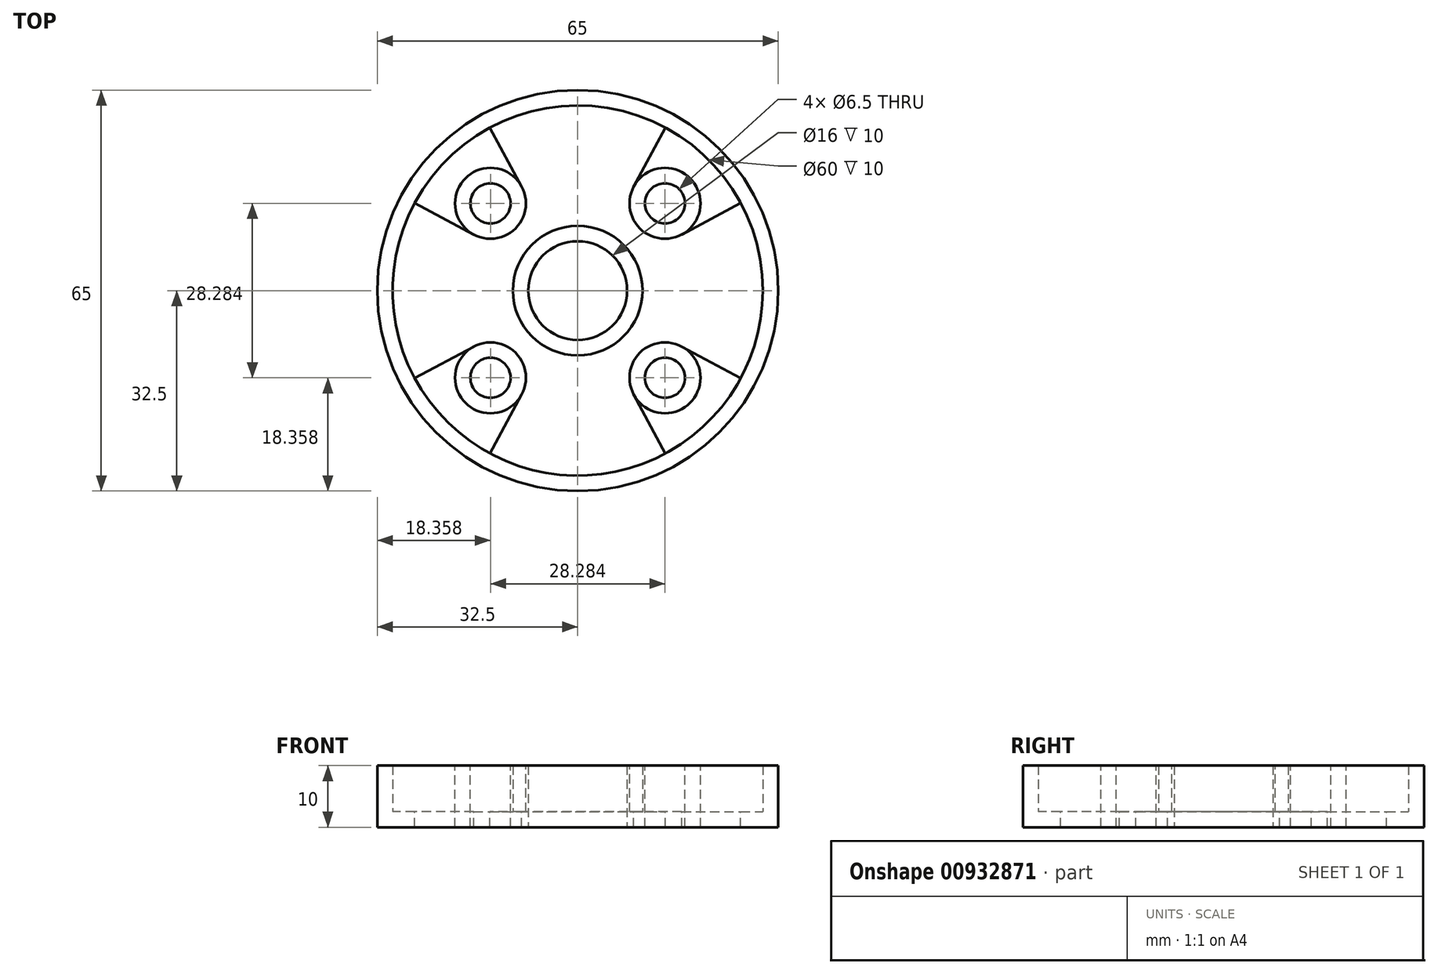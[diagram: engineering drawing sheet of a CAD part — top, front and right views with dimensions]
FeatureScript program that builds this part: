
annotation { "Feature Type Name" : "Feature", "Feature Type Description" : "" }
export const myFeature = defineFeature(function(context is Context, id is Id, definition is map)
    precondition{}
    {
        {
            var Q0;
            Q0=qCreatedBy(makeId("Top.planeOp"),FACE);
            var sketch = newSketch(context, id + "F0", { "sketchPlane" : qUnion([Q0])});
            skCircle(sketch, "E0", {"center": v(0, 0) * mm, "radius": 32.5 * mm});
            skSolve(sketch);
        }
        {
            var Q0;
            Q0 = qSketchRegion(id + "F0", true);
            extrude(context, id + "F1", {"entities" : qUnion([Q0]), "depth" : 10 * mm, "offsetDistance" : 25 * mm});
        }
        {
            var Q0;
            Q0=qCreatedBy(makeId("Top.planeOp"),FACE);
            var sketch = newSketch(context, id + "F2", { "sketchPlane" : qUnion([Q0])});
            skCircle(sketch, "E1", {"center": v(0, 0) * mm, "radius": 8 * mm});
            skSolve(sketch);
        }
        {
            var Q0;
            Q0 = qSketchRegion(id + "F2", true);
            extrude(context, id + "F3", {"entities" : qUnion([Q0]), "operationType" : NewBodyOperationType.REMOVE, "depth" : 25 * mm, "offsetDistance" : 25 * mm});
        }
        {
            var Q0;
            Q0=makeQuery(id+"F1.opExtrude","CAP_FACE",FACE,{"disambiguationData":[OSD([sQuery(id+"F0.wireOp",EDGE,"E0")])],"isStart":false});
            var sketch = newSketch(context, id + "F4", { "sketchPlane" : qUnion([Q0])});
            skCircle(sketch, "E2", {"center": v(-14.14, 14.14) * mm, "radius": 3.25 * mm});
            skCircle(sketch, "E3.MirrorC", {"center": v(-14.14, -14.14) * mm, "radius": 3.25 * mm});
            skCircle(sketch, "E4.MirrorC", {"center": v(14.14, 14.14) * mm, "radius": 3.25 * mm});
            skCircle(sketch, "E5.MirrorC", {"center": v(14.14, -14.14) * mm, "radius": 3.25 * mm});
            skSolve(sketch);
        }
        {
            var Q0;
            Q0 = qSketchRegion(id + "F4", true);
            extrude(context, id + "F5", {"entities" : qUnion([Q0]), "operationType" : NewBodyOperationType.REMOVE, "oppositeDirection" : true, "depth" : 25 * mm, "offsetDistance" : 25 * mm});
        }
        {
            var Q0;
            Q0=makeQuery(id+"F1.opExtrude","CAP_FACE",FACE,{"disambiguationData":[OSD([sQuery(id+"F0.wireOp",EDGE,"E0")])],"isStart":false});
            shell(context, id + "F6", {"entities" : qUnion([Q0]), "thickness" : 2.5 * mm});
        }
        {
            var Q0;
            {var subQ0=sQuery(id+"F0.wireOp",EDGE,"E0");Q0=makeQuery(id+"F6.opShell","OFFSET_FACE",FACE,{"disambiguationData":[OSD([subQ0]),TDD([makeQuery(id+"F1.opExtrude","CAP_FACE",FACE,{"disambiguationData":[OSD([subQ0])],"isStart":true})])]});}
            var sketch = newSketch(context, id + "F7", { "sketchPlane" : qUnion([Q0])});
            skLineSegment(sketch, "E6", {"start": v(16.87, 9.08) * mm, "end": v(26.42, 14.22) * mm});
            skLineSegment(sketch, "E7", {"start": v(9.08, 16.87) * mm, "end": v(14.22, 26.42) * mm});
            skLineSegment(sketch, "E8.MirrorCS", {"start": v(-9.08, 16.87) * mm, "end": v(-14.22, 26.42) * mm});
            skLineSegment(sketch, "E9.MirrorCS", {"start": v(-16.87, 9.08) * mm, "end": v(-26.42, 14.22) * mm});
            skLineSegment(sketch, "E10.MirrorCS", {"start": v(16.87, -9.08) * mm, "end": v(26.42, -14.22) * mm});
            skLineSegment(sketch, "E11.MirrorCS", {"start": v(9.08, -16.87) * mm, "end": v(14.22, -26.42) * mm});
            skLineSegment(sketch, "E12.MirrorCS", {"start": v(-16.87, -9.08) * mm, "end": v(-26.42, -14.22) * mm});
            skLineSegment(sketch, "E13.MirrorCS", {"start": v(-9.08, -16.87) * mm, "end": v(-14.22, -26.42) * mm});
            skSolve(sketch);
        }
        {
            var Q0;
            Q0 = qSketchRegion(id + "F7", true);
            var Q1;
            {var subQ0=sQuery(id+"F7.wireOp",EDGE,"E6");Q1=makeQuery(id+"F7.imprint","IMPRINT",FACE,{"disambiguationData":[TD([[makeQuery(id+"F7.imprint","IMPRINT",EDGE,{"derivedFrom":subQ0}),1.0]])]});}
            var Q2;
            {var subQ0=sQuery(id+"F7.wireOp",EDGE,"E8.MirrorCS");Q2=makeQuery(id+"F7.imprint","IMPRINT",FACE,{"disambiguationData":[TD([[makeQuery(id+"F7.imprint","IMPRINT",EDGE,{"derivedFrom":subQ0}),1.0]])]});}
            var Q3;
            {var subQ0=sQuery(id+"F7.wireOp",EDGE,"E10.MirrorCS");Q3=makeQuery(id+"F7.imprint","IMPRINT",FACE,{"disambiguationData":[TD([[makeQuery(id+"F7.imprint","IMPRINT",EDGE,{"derivedFrom":subQ0}),-1.0]])]});}
            var Q4;
            {var subQ0=sQuery(id+"F7.wireOp",EDGE,"E12.MirrorCS");Q4=makeQuery(id+"F7.imprint","IMPRINT",FACE,{"disambiguationData":[TD([[makeQuery(id+"F7.imprint","IMPRINT",EDGE,{"derivedFrom":subQ0}),1.0]])]});}
            extrude(context, id + "F8", {"entities" : qUnion([Q0, Q1, Q2, Q3, Q4]), "operationType" : NewBodyOperationType.REMOVE, "oppositeDirection" : true, "depth" : 25 * mm, "offsetDistance" : 25 * mm});
        }
    });
